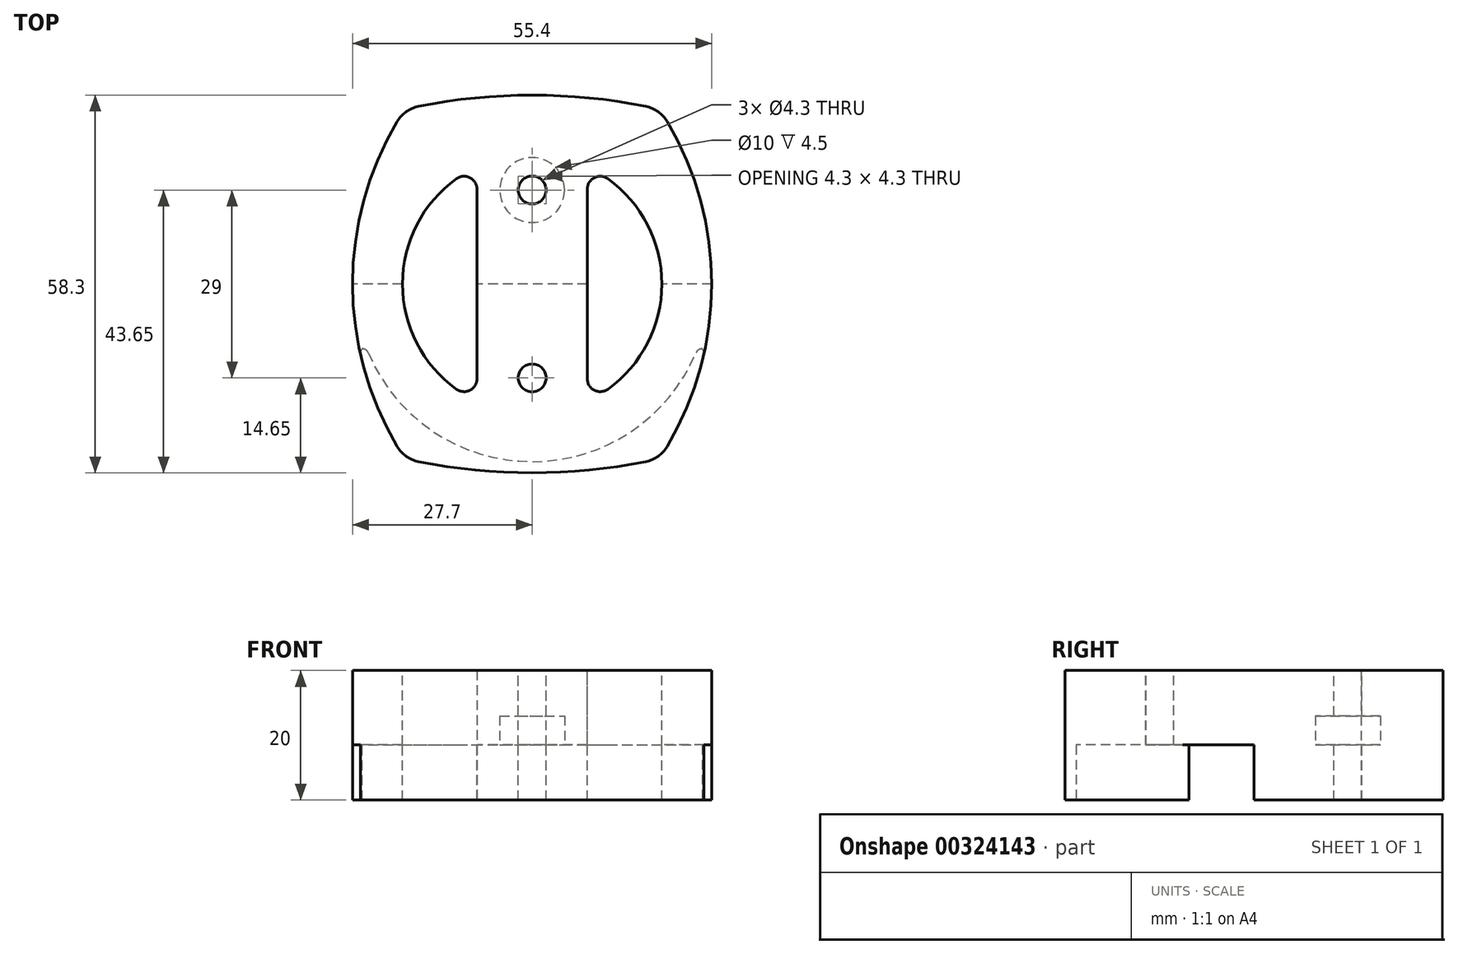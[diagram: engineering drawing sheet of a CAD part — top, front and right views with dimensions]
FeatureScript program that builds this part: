
annotation { "Feature Type Name" : "Feature", "Feature Type Description" : "" }
export const myFeature = defineFeature(function(context is Context, id is Id, definition is map)
    precondition{}
    {
        {
            var Q0;
            Q0=qCreatedBy(makeId("Top.planeOp"),FACE);
            var sketch = newSketch(context, id + "F0", { "sketchPlane" : qUnion([Q0])});
            skLineSegment(sketch, "E0.bottom", {"start": v(-28.3, 29.75) * mm, "end": v(28.3, 29.75) * mm, "construction": true});
            skLineSegment(sketch, "E0.top", {"start": v(-28.3, -29.75) * mm, "end": v(28.3, -29.75) * mm, "construction": true});
            skLineSegment(sketch, "E0.left", {"start": v(-28.3, 29.75) * mm, "end": v(-28.3, -29.75) * mm, "construction": true});
            skLineSegment(sketch, "E0.right", {"start": v(28.3, 29.75) * mm, "end": v(28.3, -29.75) * mm, "construction": true});
            skPoint(sketch, "E0.middle", {"position": v(0, 0) * mm});
            skArc(sketch, "E1", {"start": v(20, 27.5) * mm, "mid": v(0, 29.75) * mm, "end": v(-20, 27.5) * mm, "construction": true});
            skArc(sketch, "E2", {"start": v(20, -27.5) * mm, "mid": v(28.3, 0) * mm, "end": v(20, 27.5) * mm, "construction": true});
            skArc(sketch, "E3.MirrorCS", {"start": v(-20, -27.5) * mm, "mid": v(-28.3, 0) * mm, "end": v(-20, 27.5) * mm, "construction": true});
            skArc(sketch, "E4.MirrorCS", {"start": v(20, -27.5) * mm, "mid": v(0, -29.75) * mm, "end": v(-20, -27.5) * mm, "construction": true});
            skArc(sketch, "E5.0", {"start": v(19.63, -26.96) * mm, "mid": v(27.7, 0) * mm, "end": v(19.63, 26.96) * mm});
            skArc(sketch, "E5.1", {"start": v(19.63, -26.96) * mm, "mid": v(0, -29.15) * mm, "end": v(-19.63, -26.96) * mm});
            skArc(sketch, "E5.2", {"start": v(-19.63, -26.96) * mm, "mid": v(-27.7, 0) * mm, "end": v(-19.63, 26.96) * mm});
            skArc(sketch, "E5.3", {"start": v(19.63, 26.96) * mm, "mid": v(0, 29.15) * mm, "end": v(-19.63, 26.96) * mm});
            skSolve(sketch);
        }
        {
            var Q0;
            Q0=qSketchRegion(id+"F0",true);
            extrude(context, id + "F1", {"entities" : qUnion([Q0]), "depth" : 20 * mm});
        }
        {
            var Q0;
            Q0=makeQuery(id+"F0.imprint","IMPRINT",FACE,{"disambiguationData":[TD([[makeQuery(id+"F0.imprint","IMPRINT",EDGE,{"derivedFrom":sQuery(id+"F0.wireOp",EDGE,"E5.0")}),1.0]])]});
            var sketch = newSketch(context, id + "F2", { "sketchPlane" : qUnion([Q0])});
            skLineSegment(sketch, "E6.bottom", {"start": v(-11.25, -25) * mm, "end": v(11.25, -25) * mm, "construction": true});
            skLineSegment(sketch, "E6.top", {"start": v(-11.25, 25) * mm, "end": v(11.25, 25) * mm, "construction": true});
            skLineSegment(sketch, "E6.left", {"start": v(-11.25, -25) * mm, "end": v(-11.25, 25) * mm, "construction": true});
            skPoint(sketch, "E6.middle", {"position": v(0, 0) * mm});
            skLineSegment(sketch, "E7", {"start": v(11.25, -25) * mm, "end": v(11.25, 25) * mm, "construction": true});
            skLineSegment(sketch, "E8", {"start": v(0, 0) * mm, "end": v(-34.58, 0) * mm});
            skLineSegment(sketch, "E9", {"start": v(0, 0) * mm, "end": v(34.58, 0) * mm});
            skLineSegment(sketch, "E10", {"start": v(-25.53, -10) * mm, "end": v(-34.58, -10) * mm});
            skLineSegment(sketch, "E11", {"start": v(-34.58, -10) * mm, "end": v(-34.58, 0) * mm});
            skLineSegment(sketch, "E12.MirrorCS", {"start": v(25.53, -10) * mm, "end": v(34.58, -10) * mm});
            skLineSegment(sketch, "E13.MirrorCS", {"start": v(34.58, -10) * mm, "end": v(34.58, 0) * mm});
            skPoint(sketch, "E14.orphan", {"position": v(38.67, 0) * mm});
            skArc(sketch, "E15.trimOffspring", {"start": v(-25.53, -10) * mm, "mid": v(0, -27.41) * mm, "end": v(25.53, -10) * mm});
            skSolve(sketch);
        }
        {
            var Q0;
            Q0=qSketchRegion(id+"F2",true);
            extrude(context, id + "F3", {"entities" : qUnion([Q0]), "operationType" : NewBodyOperationType.REMOVE, "depth" : 8.5 * mm});
        }
        {
            var Q0;
            Q0=qCreatedBy(makeId("Right.planeOp"),FACE);
            var sketch = newSketch(context, id + "F4", { "sketchPlane" : qUnion([Q0])});
            skLineSegment(sketch, "E16", {"start": v(0, -20.7) * mm, "end": v(0, 46.83) * mm});
            skSolve(sketch);
        }
        {
            var Q0;
            Q0=makeQuery(id+"F1.opExtrude","CAP_FACE",FACE,{"disambiguationData":[OSD([sQuery(id+"F0.wireOp",EDGE,"E5.0"),sQuery(id+"F0.wireOp",EDGE,"E5.1"),sQuery(id+"F0.wireOp",EDGE,"E5.2"),sQuery(id+"F0.wireOp",EDGE,"E5.3")])],"isStart":false});
            var sketch = newSketch(context, id + "F5", { "sketchPlane" : qUnion([Q0])});
            skCircle(sketch, "E17", {"center": v(0, -14.5) * mm, "radius": 2.15 * mm});
            skCircle(sketch, "E18", {"center": v(0, 14.5) * mm, "radius": 2.15 * mm});
            skSolve(sketch);
        }
        {
            var Q0;
            Q0=makeQuery(id+"F5.imprint","IMPRINT",FACE,{"disambiguationData":[TD([[makeQuery(id+"F5.imprint","IMPRINT",EDGE,{"derivedFrom":sQuery(id+"F5.wireOp",EDGE,"E17")}),1.0]])]});
            var Q1;
            Q1=makeQuery(id+"F5.imprint","IMPRINT",FACE,{"disambiguationData":[TD([[makeQuery(id+"F5.imprint","IMPRINT",EDGE,{"derivedFrom":sQuery(id+"F5.wireOp",EDGE,"E18")}),1.0]])]});
            extrude(context, id + "F6", {"entities" : qUnion([Q0, Q1]), "operationType" : NewBodyOperationType.REMOVE, "oppositeDirection" : true, "depth" : 25 * mm});
        }
        {
            var Q0;
            Q0=makeQuery(id+"F1.opExtrude","SWEPT_EDGE",EDGE,{"disambiguationData":[OSD([sQuery(id+"F0.wireOp",EDGE,"E5.0"),sQuery(id+"F0.wireOp",EDGE,"E5.1")])]});
            var Q1;
            Q1=makeQuery(id+"F1.opExtrude","SWEPT_EDGE",EDGE,{"disambiguationData":[OSD([sQuery(id+"F0.wireOp",EDGE,"E5.1"),sQuery(id+"F0.wireOp",EDGE,"E5.2")])]});
            var Q2;
            Q2=makeQuery(id+"F1.opExtrude","SWEPT_EDGE",EDGE,{"disambiguationData":[OSD([sQuery(id+"F0.wireOp",EDGE,"E5.2"),sQuery(id+"F0.wireOp",EDGE,"E5.3")])]});
            var Q3;
            Q3=makeQuery(id+"F1.opExtrude","SWEPT_EDGE",EDGE,{"disambiguationData":[OSD([sQuery(id+"F0.wireOp",EDGE,"E5.0"),sQuery(id+"F0.wireOp",EDGE,"E5.3")])]});
            fillet(context, id + "F7", {"entities" : qUnion([Q0, Q1, Q2, Q3]), "radius" : 5 * mm, "tangentPropagation" : true, "allowEdgeOverflow" : false});
        }
        {
            var Q0;
            Q0=makeQuery(id+"F3.boolean.opBoolean","COPY",EDGE,{"derivedFrom":makeQuery(id+"F3.opExtrude","SWEPT_EDGE",EDGE,{"disambiguationData":[OSD([sQuery(id+"F2.wireOp",EDGE,"E10"),sQuery(id+"F2.wireOp",EDGE,"E15.trimOffspring")])]})});
            var Q1;
            Q1=makeQuery(id+"FNHx4nqmU4KoeVX_1.1.F3.boolean.opBoolean","COPY",EDGE,{"derivedFrom":makeQuery(id+"FNHx4nqmU4KoeVX_1.1.F3.opExtrude","SWEPT_EDGE",EDGE,{"disambiguationData":[OSD([sQuery(id+"F2.wireOp",EDGE,"E12.MirrorCS"),sQuery(id+"F2.wireOp",EDGE,"E15.trimOffspring")])]})});
            var Q2;
            Q2=makeQuery(id+"FNHx4nqmU4KoeVX_1.1.F3.boolean.opBoolean","COPY",EDGE,{"derivedFrom":makeQuery(id+"FNHx4nqmU4KoeVX_1.1.F3.opExtrude","SWEPT_EDGE",EDGE,{"disambiguationData":[OSD([sQuery(id+"F2.wireOp",EDGE,"E10"),sQuery(id+"F2.wireOp",EDGE,"E15.trimOffspring")])]})});
            var Q3;
            Q3=makeQuery(id+"F3.boolean.opBoolean","COPY",EDGE,{"derivedFrom":makeQuery(id+"F3.opExtrude","SWEPT_EDGE",EDGE,{"disambiguationData":[OSD([sQuery(id+"F2.wireOp",EDGE,"E12.MirrorCS"),sQuery(id+"F2.wireOp",EDGE,"E15.trimOffspring")])]})});
            fillet(context, id + "F8", {"entities" : qUnion([Q0, Q1, Q2, Q3]), "radius" : 1 * mm, "tangentPropagation" : true, "allowEdgeOverflow" : false});
        }
        {
            var Q0;
            Q0=makeQuery(id+"F3.boolean.opBoolean","INTERSECT",EDGE,{"derivedFrom":[makeQuery(id+"F1.opExtrude","SWEPT_FACE",FACE,{"disambiguationData":[OSD([sQuery(id+"F0.wireOp",EDGE,"E5.2")])]}),makeQuery(id+"F3.opExtrude","SWEPT_FACE",FACE,{"disambiguationData":[OSD([sQuery(id+"F2.wireOp",EDGE,"E10")])]})]});
            var Q1;
            Q1=makeQuery(id+"F3.boolean.opBoolean","INTERSECT",EDGE,{"derivedFrom":[makeQuery(id+"F1.opExtrude","SWEPT_FACE",FACE,{"disambiguationData":[OSD([sQuery(id+"F0.wireOp",EDGE,"E5.0")])]}),makeQuery(id+"F3.opExtrude","SWEPT_FACE",FACE,{"disambiguationData":[OSD([sQuery(id+"F2.wireOp",EDGE,"E12.MirrorCS")])]})]});
            var Q2;
            Q2=makeQuery(id+"FNHx4nqmU4KoeVX_1.1.F3.boolean.opBoolean","INTERSECT",EDGE,{"derivedFrom":[makeQuery(id+"F1.opExtrude","SWEPT_FACE",FACE,{"disambiguationData":[OSD([sQuery(id+"F0.wireOp",EDGE,"E5.0")])]}),makeQuery(id+"FNHx4nqmU4KoeVX_1.1.F3.opExtrude","SWEPT_FACE",FACE,{"disambiguationData":[OSD([sQuery(id+"F2.wireOp",EDGE,"E10")])]})]});
            var Q3;
            Q3=makeQuery(id+"FNHx4nqmU4KoeVX_1.1.F3.boolean.opBoolean","INTERSECT",EDGE,{"derivedFrom":[makeQuery(id+"F1.opExtrude","SWEPT_FACE",FACE,{"disambiguationData":[OSD([sQuery(id+"F0.wireOp",EDGE,"E5.2")])]}),makeQuery(id+"FNHx4nqmU4KoeVX_1.1.F3.opExtrude","SWEPT_FACE",FACE,{"disambiguationData":[OSD([sQuery(id+"F2.wireOp",EDGE,"E12.MirrorCS")])]})]});
            fillet(context, id + "F9", {"entities" : qUnion([Q0, Q1, Q2, Q3]), "radius" : 1 * mm, "tangentPropagation" : true, "allowEdgeOverflow" : false});
        }
        {
            var Q0;
            Q0=makeQuery(id+"F1.opExtrude","CAP_FACE",FACE,{"disambiguationData":[OSD([sQuery(id+"F0.wireOp",EDGE,"E5.0"),sQuery(id+"F0.wireOp",EDGE,"E5.1"),sQuery(id+"F0.wireOp",EDGE,"E5.2"),sQuery(id+"F0.wireOp",EDGE,"E5.3")])],"isStart":false});
            var sketch = newSketch(context, id + "F10", { "sketchPlane" : qUnion([Q0])});
            skArc(sketch, "E19", {"start": v(-8.5, 18.1) * mm, "mid": v(-20, 0) * mm, "end": v(-8.5, -18.1) * mm});
            skLineSegment(sketch, "E20", {"start": v(-8.5, -18.1) * mm, "end": v(-8.5, 18.1) * mm});
            skLineSegment(sketch, "E21.MirrorCS", {"start": v(8.5, -18.1) * mm, "end": v(8.5, 18.1) * mm});
            skArc(sketch, "E22.MirrorCS", {"start": v(8.5, 18.1) * mm, "mid": v(20, 0) * mm, "end": v(8.5, -18.1) * mm});
            skSolve(sketch);
        }
        {
            var Q0;
            Q0=qSketchRegion(id+"F10",true);
            extrude(context, id + "F11", {"entities" : qUnion([Q0]), "operationType" : NewBodyOperationType.REMOVE, "oppositeDirection" : true, "depth" : 25 * mm});
        }
        {
            var Q0;
            {var subQ0=sQuery(id+"F10.wireOp",EDGE,"E20");var subQ1=sQuery(id+"F10.wireOp",EDGE,"E19");Q0=makeQuery(id+"F11.boolean.opBoolean","COPY",EDGE,{"derivedFrom":makeQuery(id+"F11.opExtrude","SWEPT_EDGE",EDGE,{"disambiguationData":[OSD([subQ1,subQ0]),TDD([makeQuery(id+"F10.imprint","INTERSECT",VERTEX,{"disambiguationData":[OD(1.0)],"derivedFrom":[subQ1,subQ0]})])]})});}
            var Q1;
            {var subQ0=sQuery(id+"F10.wireOp",EDGE,"E22.MirrorCS");var subQ1=sQuery(id+"F10.wireOp",EDGE,"E21.MirrorCS");Q1=makeQuery(id+"F11.boolean.opBoolean","COPY",EDGE,{"derivedFrom":makeQuery(id+"F11.opExtrude","SWEPT_EDGE",EDGE,{"disambiguationData":[OSD([subQ1,subQ0]),TDD([makeQuery(id+"F10.imprint","INTERSECT",VERTEX,{"disambiguationData":[OD(0.0)],"derivedFrom":[subQ1,subQ0]})])]})});}
            var Q2;
            {var subQ0=sQuery(id+"F10.wireOp",EDGE,"E20");var subQ1=sQuery(id+"F10.wireOp",EDGE,"E19");Q2=makeQuery(id+"F11.boolean.opBoolean","COPY",EDGE,{"derivedFrom":makeQuery(id+"F11.opExtrude","SWEPT_EDGE",EDGE,{"disambiguationData":[OSD([subQ1,subQ0]),TDD([makeQuery(id+"F10.imprint","INTERSECT",VERTEX,{"disambiguationData":[OD(0.0)],"derivedFrom":[subQ1,subQ0]})])]})});}
            var Q3;
            {var subQ0=sQuery(id+"F10.wireOp",EDGE,"E22.MirrorCS");var subQ1=sQuery(id+"F10.wireOp",EDGE,"E21.MirrorCS");Q3=makeQuery(id+"F11.boolean.opBoolean","COPY",EDGE,{"derivedFrom":makeQuery(id+"F11.opExtrude","SWEPT_EDGE",EDGE,{"disambiguationData":[OSD([subQ1,subQ0]),TDD([makeQuery(id+"F10.imprint","INTERSECT",VERTEX,{"disambiguationData":[OD(1.0)],"derivedFrom":[subQ1,subQ0]})])]})});}
            fillet(context, id + "F12", {"entities" : qUnion([Q0, Q1, Q2, Q3]), "radius" : 2 * mm, "tangentPropagation" : true, "allowEdgeOverflow" : false});
        }
        {
            var Q0;
            {var subQ0=sQuery(id+"F2.wireOp",EDGE,"E15.trimOffspring");var subQ1=sQuery(id+"F2.wireOp",EDGE,"E13.MirrorCS");var subQ2=sQuery(id+"F2.wireOp",EDGE,"E12.MirrorCS");var subQ3=sQuery(id+"F2.wireOp",EDGE,"E11");var subQ4=sQuery(id+"F2.wireOp",EDGE,"E10");var subQ5=sQuery(id+"F2.wireOp",EDGE,"E9");var subQ6=sQuery(id+"F2.wireOp",EDGE,"E8");Q0=makeQuery(id+"FNHx4nqmU4KoeVX_1.1.F3.boolean.opBoolean","MERGE",FACE,{"derivedFrom":[makeQuery(id+"F3.boolean.opBoolean","COPY",FACE,{"derivedFrom":makeQuery(id+"F3.opExtrude","CAP_FACE",FACE,{"disambiguationData":[OSD([subQ6,subQ5,subQ4,subQ3,subQ2,subQ1,subQ0])],"isStart":false})}),makeQuery(id+"FNHx4nqmU4KoeVX_1.1.F3.opExtrude","CAP_FACE",FACE,{"disambiguationData":[OSD([subQ6,subQ5,subQ4,subQ3,subQ2,subQ1,subQ0])],"isStart":false})]});}
            var sketch = newSketch(context, id + "F13", { "sketchPlane" : qUnion([Q0])});
            skCircle(sketch, "E23", {"center": v(0, -14.5) * mm, "radius": 5 * mm});
            skSolve(sketch);
        }
        {
            var Q0;
            Q0=qSketchRegion(id+"F13",true);
            extrude(context, id + "F14", {"entities" : qUnion([Q0]), "operationType" : NewBodyOperationType.REMOVE, "oppositeDirection" : true, "depth" : 4.5 * mm});
        }
    });
